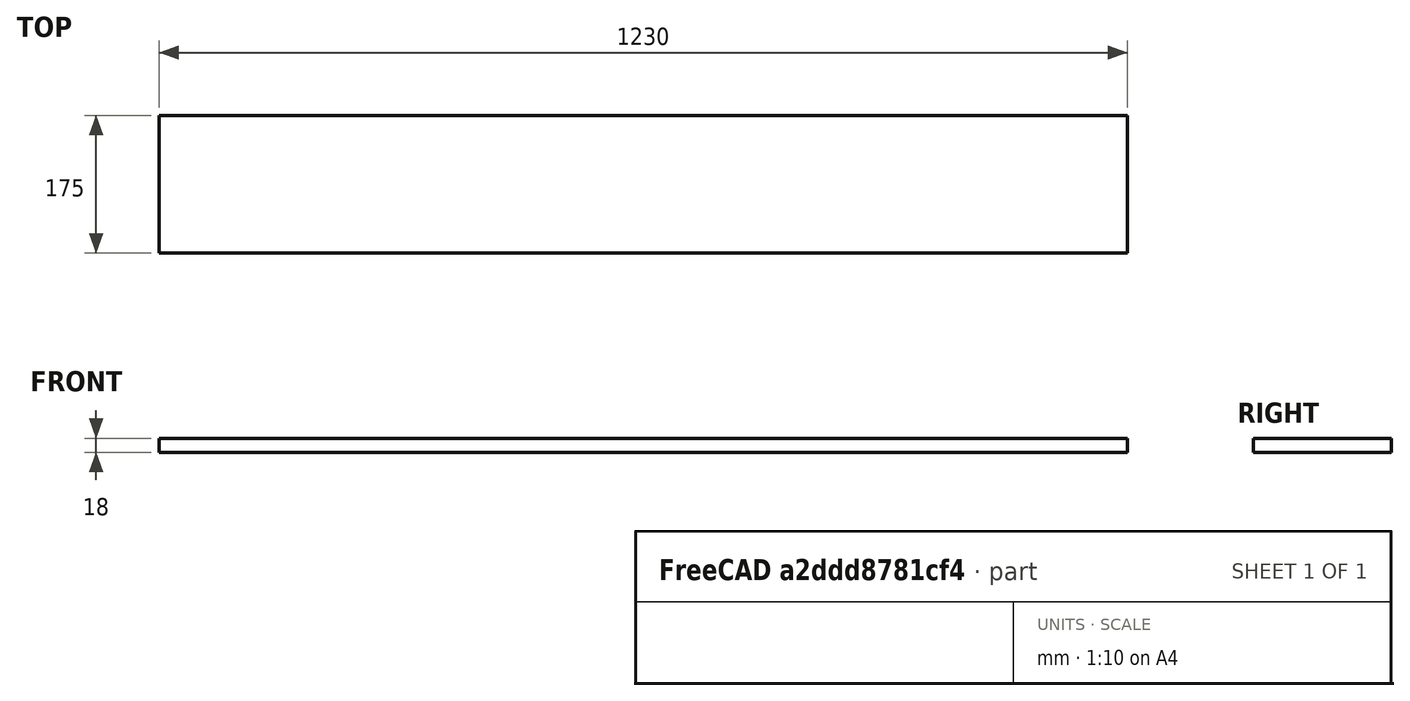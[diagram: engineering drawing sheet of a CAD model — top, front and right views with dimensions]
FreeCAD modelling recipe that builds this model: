
FCSTD DOCUMENT  (FreeCAD 1.0R39109 (Git))
Label: 12_shelf_top_down
License: All rights reserved
LicenseURL: http://en.wikipedia.org/wiki/All_rights_reserved
objects: Spreadsheet::Sheet×1, Sketcher::SketchObject×1, PartDesign::Pad×1, PartDesign::Body×1
note: 6 computed .brp shape members not serialized (recipe doc carries the construction recipe); baked Part::Feature solids carry a one-line shape summary decoded from their .brp

FEATURE [Spreadsheet::Sheet] Spreadsheet
  cells = A2='length; B2(length)=1230; A3='width; B3(width)=175; A4='height; B4(height)=18
FEATURE [Sketcher::SketchObject] Sketch
  ArcFitTolerance = 0
  AttachmentSupport = -> [XY_Plane]
  FullyConstrained = true
  MakeInternals = false
  MapMode = 5
  expr: Constraints[11] = Spreadsheet.length
  expr: Constraints[12] = Spreadsheet.width
  sketch-geometry (5):
    g0: LineSegment StartX=-615 StartY=87.5 StartZ=0 EndX=615 EndY=87.5 EndZ=0
    g1: LineSegment StartX=615 StartY=87.5 StartZ=0 EndX=615 EndY=-87.5 EndZ=0
    g2: LineSegment StartX=615 StartY=-87.5 StartZ=0 EndX=-615 EndY=-87.5 EndZ=0
    g3: LineSegment StartX=-615 StartY=-87.5 StartZ=0 EndX=-615 EndY=87.5 EndZ=0
    g4: LineSegment [constr] StartX=-615 StartY=87.5 StartZ=0 EndX=615 EndY=-87.5 EndZ=0
  constraints (13):
    c: Coincident(g0,g1)
    c: Coincident(g1,g2)
    c: Coincident(g2,g3)
    c: Coincident(g3,g0)
    c: Horizontal(g0)
    c: Horizontal(g2)
    c: Vertical(g1)
    c: Vertical(g3)
    c: Coincident(g4,g1)
    c: Coincident(g0,g4)
    c: Symmetric(g0,g1,g-1)
    c: Distance(g0,g0) = 1230
    c: Distance(g0,g2) = 175
FEATURE [PartDesign::Pad] Pad
  Direction = (0,0,1)
  Length = 18
  Length2 = 10
  Profile = -> Sketch
  ReferenceAxis = -> Sketch [N_Axis]
  Suppressed = false
  Type = 0
  expr: Length = Spreadsheet.height
FEATURE [PartDesign::Body] Body
  AllowCompound = false
  Group = -> [Sketch,Pad]
  Origin = -> Origin
  Tip = -> Pad
